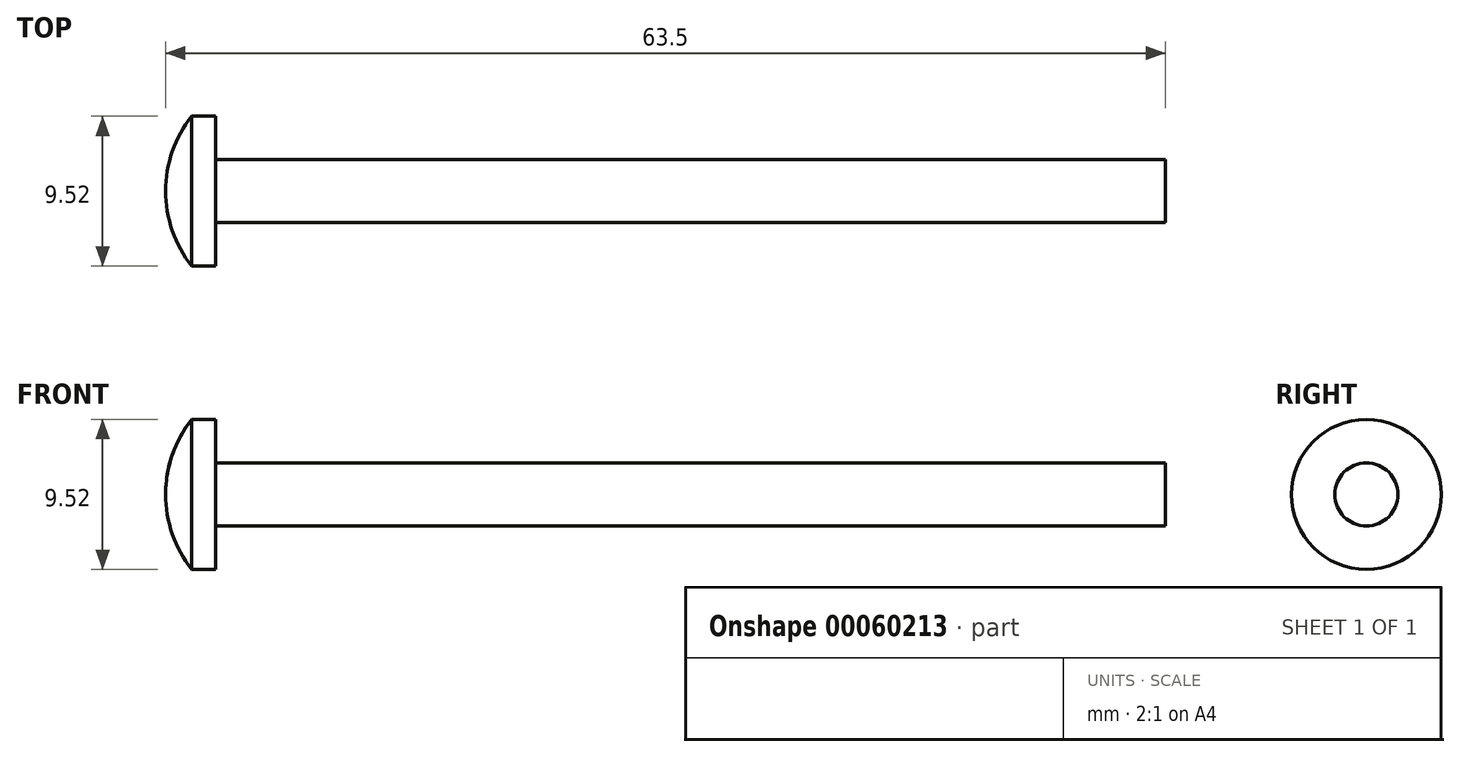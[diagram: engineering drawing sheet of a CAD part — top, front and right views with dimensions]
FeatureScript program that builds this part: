
annotation { "Feature Type Name" : "Feature", "Feature Type Description" : "" }
export const myFeature = defineFeature(function(context is Context, id is Id, definition is map)
    precondition{}
    {
        {
            var Q0;
            Q0=qCreatedBy(makeId("Front.planeOp"),FACE);
            var sketch = newSketch(context, id + "F0", { "sketchPlane" : qUnion([Q0])});
            skLineSegment(sketch, "E0", {"start": v(28.6, 0) * mm, "end": v(-9.6, 0) * mm, "construction": true});
            skLineSegment(sketch, "E1", {"start": v(0, 4.76) * mm, "end": v(0, 2) * mm});
            skLineSegment(sketch, "E2", {"start": v(0, 2) * mm, "end": v(60.33, 2) * mm});
            skLineSegment(sketch, "E3", {"start": v(60.33, 2) * mm, "end": v(60.33, 0) * mm});
            skLineSegment(sketch, "E4", {"start": v(0, 4.76) * mm, "end": v(-1.52, 4.76) * mm});
            skLineSegment(sketch, "E5", {"start": v(-3.17, 0) * mm, "end": v(-3.17, -2.39) * mm, "construction": true});
            skArc(sketch, "E6", {"start": v(-3.17, 0) * mm, "mid": v(-2.75, 2.52) * mm, "end": v(-1.52, 4.76) * mm});
            skLineSegment(sketch, "E7", {"start": v(-3.17, 0) * mm, "end": v(60.33, 0) * mm});
            skSolve(sketch);
        }
        {
            var Q0;
            Q0=makeQuery(id+"F0.imprint","IMPRINT",FACE,{"disambiguationData":[TD([[makeQuery(id+"F0.imprint","IMPRINT",EDGE,{"derivedFrom":sQuery(id+"F0.wireOp",EDGE,"E1")}),-1.0]])]});
            var Q1;
            Q1=sQuery(id+"F0.wireOp",EDGE,"E0");
            revolve(context, id + "F1", {"entities" : qUnion([Q0]), "axis" : qUnion([Q1]), "revolveType" : RevolveType.FULL});
        }
    });
